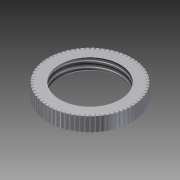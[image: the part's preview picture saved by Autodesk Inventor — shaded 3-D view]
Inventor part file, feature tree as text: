
AUTODESK INVENTOR PART (.ipt)
format: ipt  version: 2011 SP1 (Build 150282100, 282)  size: 337,408 bytes
history: native  units: in
note: dims shown in document units (in); Inventor stores cm internally (conversion verified against a paired STEP export)
features: other x14, sketch x3, extrude x2, hole x1
ambient origin geometry x8: Origin, YZ Plane, XZ Plane, XY Plane, X Axis, Y Axis, Z Axis, Center Point
bodies: Solid1 (feature_tree)
feature tree (20):
  extrude  "Extrusion1"  Depth=0.098in TaperAngle=0.0deg
  hole  "Drilling 1"  [1 undecoded]
  extrude  "Extrusion2"  [1 undecoded]
  other  "b_XY"
  other  "b_YZ"
  other  "b_ZX"
  other  "b_X"
  other  "b_Y"
  other  "b_Z"
  other  "b_Center"
  other  "t_XY"
  other  "t_YZ"
  other  "t_ZX"
  other  "t_X"
  other  "t_Y"
  other  "t_Z"
  other  "t_Center"
  sketch  "Sketch_1"  dims[d0=0.098in d1=0.0in]
  sketch  "Sketch2"  dims[d2=0.4298in d3=0.098in d4=0.4724in d5=0.25in d6=0.6184in d7=0.098in d8=0.0in d9=0.098in d10=0.0in]
  sketch  "Sketch_3"
note: 2 required parameter values undecoded (feature->parameter linkage not recoverable at this tier; creation-order binding heuristic only, values carry confidence <= 0.55)
